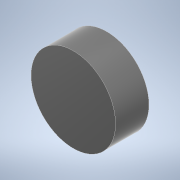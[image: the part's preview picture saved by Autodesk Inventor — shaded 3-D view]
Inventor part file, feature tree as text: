
AUTODESK INVENTOR PART (.ipt)
format: ipt  version: 2022 (Build 260153000, 153)  size: 224,256 bytes
history: native  units: mm
features: other x1, extrude x1, sketch x1
ambient origin geometry x8: Origin, YZ Plane, XZ Plane, XY Plane, X Axis, Y Axis, Z Axis, Center Point
bodies: Body1 (feature_tree)
feature tree (3):
  other  "Sólido1"
  extrude  "Extrusión1"  Depth=1.5mm TaperAngle=0.0deg
  sketch  "Boceto1"  dims[d0=3.8mm d1=1.5mm d2=0.0mm]
